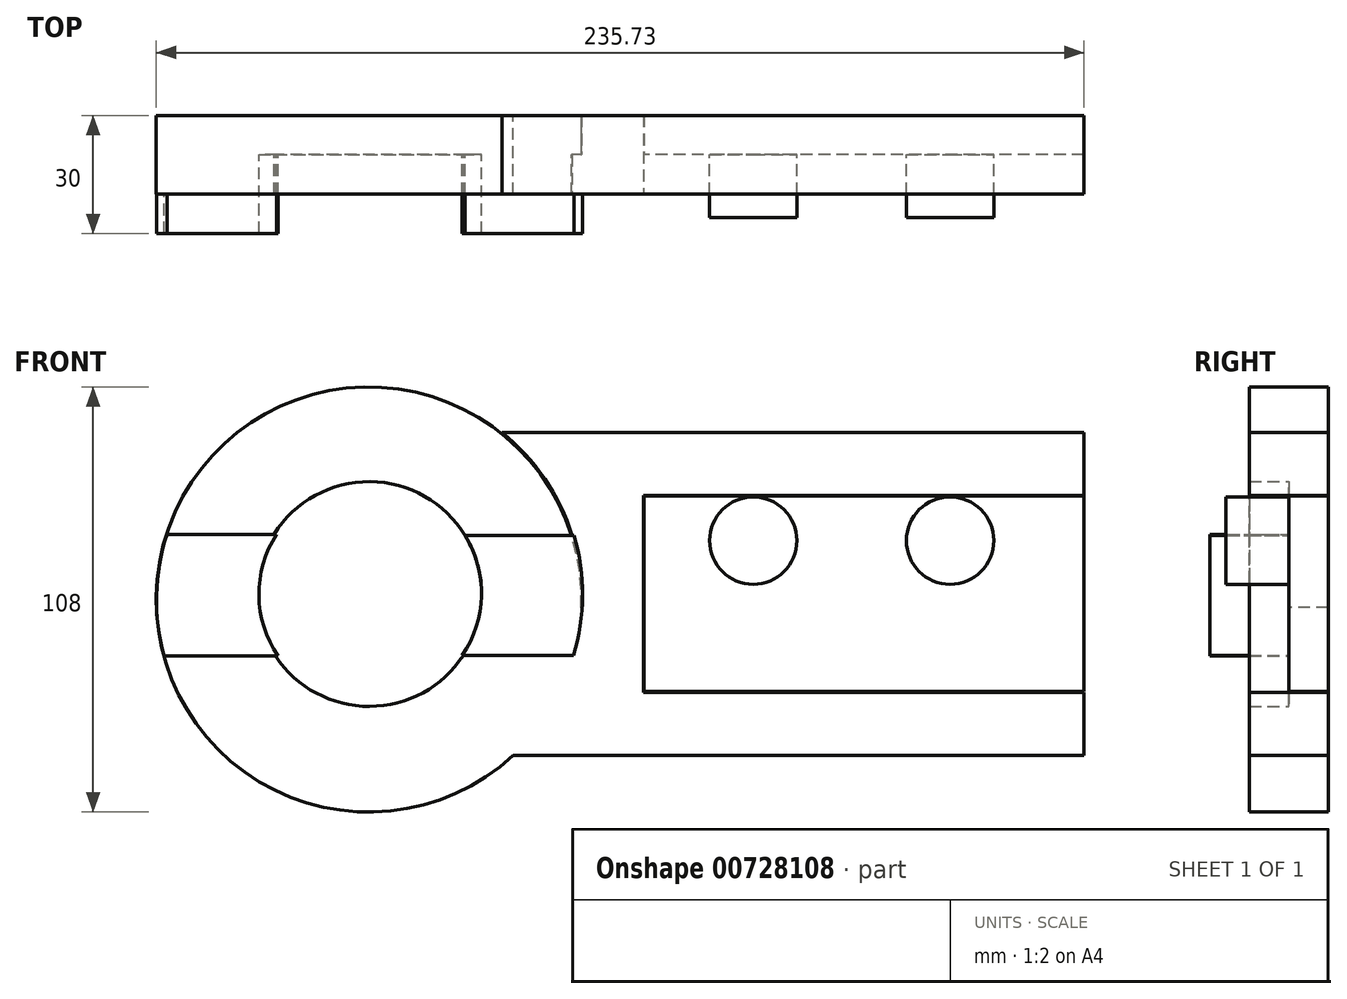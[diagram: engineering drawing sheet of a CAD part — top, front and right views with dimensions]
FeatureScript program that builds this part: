
annotation { "Feature Type Name" : "Feature", "Feature Type Description" : "" }
export const myFeature = defineFeature(function(context is Context, id is Id, definition is map)
    precondition{}
    {
        {
            var Q0;
            Q0=qCreatedBy(makeId("Front.planeOp"),FACE);
            var sketch = newSketch(context, id + "F0", { "sketchPlane" : qUnion([Q0])});
            skLineSegment(sketch, "E0", {"start": v(0, 0) * mm, "end": v(-52.16, 0) * mm});
            skCircle(sketch, "E1", {"center": v(-52.16, -1.4) * mm, "radius": 54 * mm});
            skSolve(sketch);
        }
        {
            var Q0;
            Q0 = qSketchRegion(id + "F0", true);
            extrude(context, id + "F1", {"entities" : qUnion([Q0]), "endBound" : BoundingType.SYMMETRIC, "depth" : 20 * mm, "offsetDistance" : 25 * mm});
        }
        {
            var Q0;
            Q0=qCreatedBy(makeId("Front.planeOp"),FACE);
            var sketch = newSketch(context, id + "F2", { "sketchPlane" : qUnion([Q0])});
            skLineSegment(sketch, "E2", {"start": v(0, 0) * mm, "end": v(-52.06, 0) * mm});
            skCircle(sketch, "E3", {"center": v(-52.06, 0) * mm, "radius": 28.55 * mm});
            skSolve(sketch);
        }
        {
            var Q0;
            Q0 = qSketchRegion(id + "F2", true);
            extrude(context, id + "F3", {"entities" : qUnion([Q0]), "operationType" : NewBodyOperationType.REMOVE, "depth" : 25 * mm, "offsetDistance" : 25 * mm});
        }
        {
            var Q0;
            Q0=qCreatedBy(makeId("Front.planeOp"),FACE);
            var sketch = newSketch(context, id + "F4", { "sketchPlane" : qUnion([Q0])});
            skArc(sketch, "E4", {"start": v(-75.18, -15.77) * mm, "mid": v(-80.07, -0.35) * mm, "end": v(-75.56, 15.2) * mm});
            skLineSegment(sketch, "E5", {"start": v(-75.56, 15.2) * mm, "end": v(-103.38, 15.2) * mm});
            skLineSegment(sketch, "E6", {"start": v(-75.18, -15.77) * mm, "end": v(-104.13, -15.77) * mm});
            skArc(sketch, "E7", {"start": v(-103.38, 15.2) * mm, "mid": v(-106.08, -0.23) * mm, "end": v(-104.13, -15.77) * mm});
            skArc(sketch, "E8", {"start": v(-27.69, 14.84) * mm, "mid": v(-23.54, -0.48) * mm, "end": v(-28.44, -15.58) * mm});
            skLineSegment(sketch, "E9", {"start": v(-28.44, -15.58) * mm, "end": v(-0.18, -15.58) * mm});
            skLineSegment(sketch, "E10", {"start": v(-27.69, 14.84) * mm, "end": v(0, 14.84) * mm});
            skArc(sketch, "E11", {"start": v(-0.18, -15.58) * mm, "mid": v(2.15, -0.39) * mm, "end": v(0, 14.84) * mm});
            skSolve(sketch);
        }
        {
            var Q0;
            Q0 = qSketchRegion(id + "F4", true);
            extrude(context, id + "F5", {"entities" : qUnion([Q0]), "operationType" : NewBodyOperationType.ADD, "depth" : 20 * mm, "offsetDistance" : 25 * mm});
        }
        {
            var Q0;
            Q0=qCreatedBy(makeId("Front.planeOp"),FACE);
            var sketch = newSketch(context, id + "F6", { "sketchPlane" : qUnion([Q0])});
            skLineSegment(sketch, "E12", {"start": v(17.57, 0) * mm, "end": v(17.57, 25) * mm});
            skLineSegment(sketch, "E13", {"start": v(17.57, 0) * mm, "end": v(17.57, -25) * mm});
            skLineSegment(sketch, "E14", {"start": v(17.57, 25) * mm, "end": v(129.57, 25) * mm});
            skLineSegment(sketch, "E15", {"start": v(17.57, -25) * mm, "end": v(129.57, -25) * mm});
            skLineSegment(sketch, "E16", {"start": v(129.57, 25) * mm, "end": v(129.57, 41) * mm});
            skLineSegment(sketch, "E17", {"start": v(129.57, 41) * mm, "end": v(-18.35, 41) * mm});
            skLineSegment(sketch, "E18", {"start": v(-16.34, -41.02) * mm, "end": v(129.57, -41.02) * mm});
            skLineSegment(sketch, "E19", {"start": v(129.57, -41.02) * mm, "end": v(129.57, -25) * mm});
            skArc(sketch, "E20", {"start": v(-16.34, -41.02) * mm, "mid": v(1.85, 0.46) * mm, "end": v(-18.35, 41) * mm});
            skSolve(sketch);
        }
        {
            var Q0;
            Q0 = qSketchRegion(id + "F6", true);
            extrude(context, id + "F7", {"entities" : qUnion([Q0]), "operationType" : NewBodyOperationType.ADD, "endBound" : BoundingType.SYMMETRIC, "oppositeDirection" : true, "depth" : 20 * mm, "offsetDistance" : 25 * mm});
        }
        {
            var Q0;
            Q0=qCreatedBy(makeId("Front.planeOp"),FACE);
            var sketch = newSketch(context, id + "F8", { "sketchPlane" : qUnion([Q0])});
            skCircle(sketch, "E21", {"center": v(45.51, 13.58) * mm, "radius": 11.1 * mm});
            skCircle(sketch, "E22", {"center": v(95.51, 13.58) * mm, "radius": 11.1 * mm});
            skSolve(sketch);
        }
        {
            var Q0;
            Q0 = qSketchRegion(id + "F8", true);
            extrude(context, id + "F9", {"entities" : qUnion([Q0]), "depth" : 16 * mm, "offsetDistance" : 25 * mm});
        }
        {
            var Q0;
            Q0=qCreatedBy(makeId("Front.planeOp"),FACE);
            var sketch = newSketch(context, id + "F10", { "sketchPlane" : qUnion([Q0])});
            skLineSegment(sketch, "E23", {"start": v(17.74, -24.73) * mm, "end": v(17.74, 24.91) * mm});
            skLineSegment(sketch, "E24", {"start": v(17.74, 24.91) * mm, "end": v(129.52, 24.91) * mm});
            skLineSegment(sketch, "E25", {"start": v(129.52, 24.91) * mm, "end": v(129.52, -24.73) * mm});
            skLineSegment(sketch, "E26", {"start": v(129.52, -24.73) * mm, "end": v(17.74, -24.73) * mm});
            skSolve(sketch);
        }
        {
            var Q0;
            Q0 = qSketchRegion(id + "F10", true);
            extrude(context, id + "F11", {"entities" : qUnion([Q0]), "oppositeDirection" : true, "depth" : 10 * mm, "offsetDistance" : 25 * mm});
        }
    });
